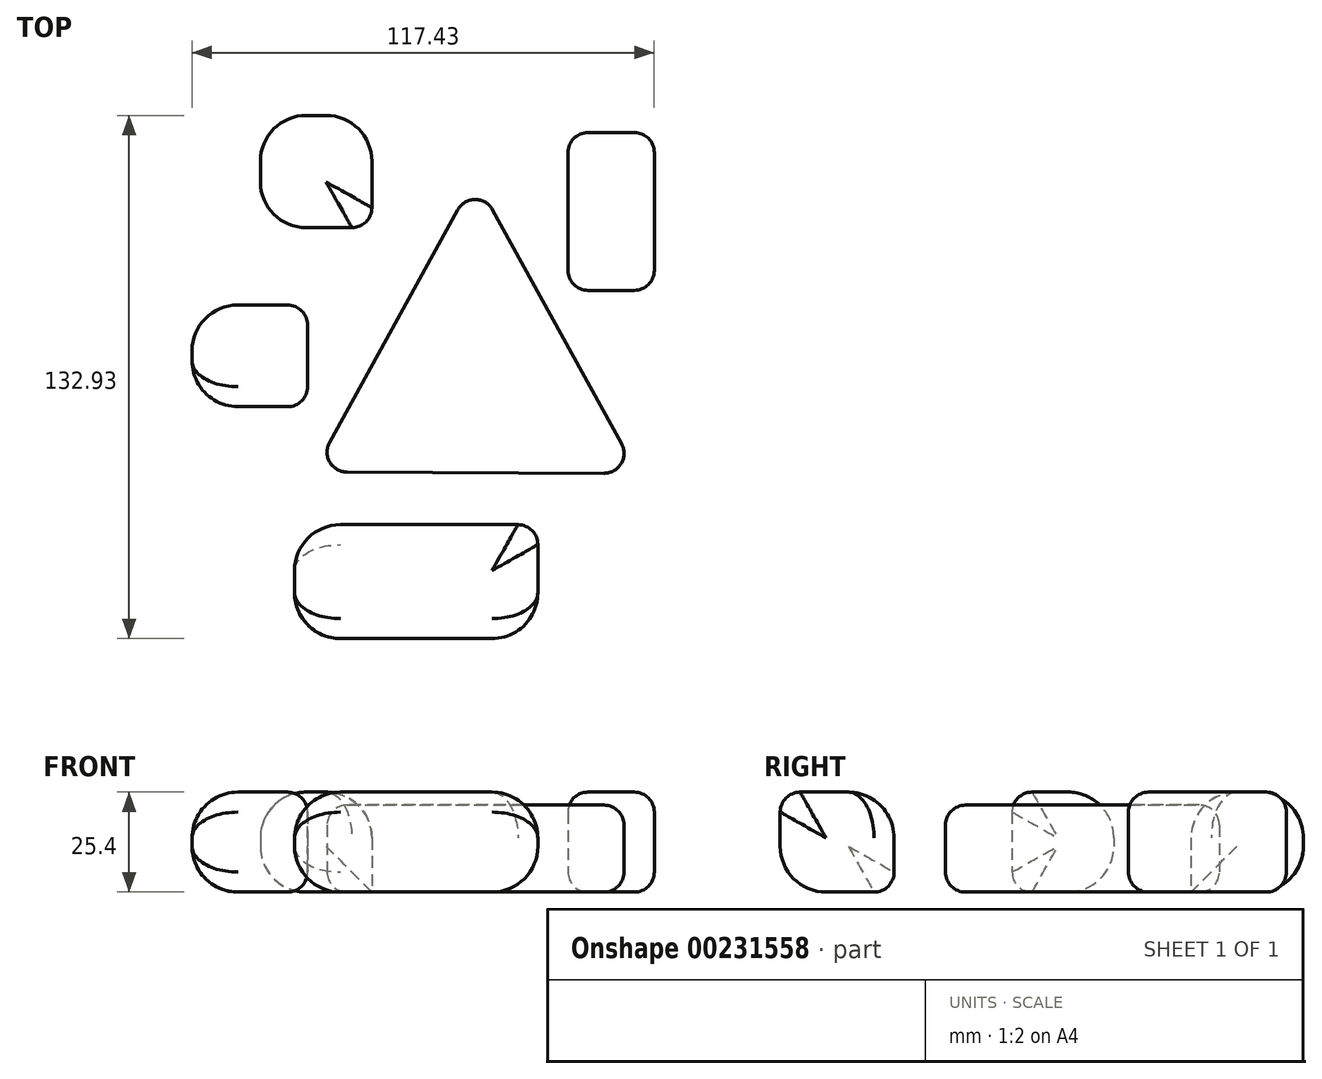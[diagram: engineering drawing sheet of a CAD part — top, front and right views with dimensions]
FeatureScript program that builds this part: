
annotation { "Feature Type Name" : "Feature", "Feature Type Description" : "" }
export const myFeature = defineFeature(function(context is Context, id is Id, definition is map)
    precondition{}
    {
        {
            var Q0;
            Q0=qCreatedBy(makeId("Top.planeOp"),FACE);
            var sketch = newSketch(context, id + "F0", { "sketchPlane" : qUnion([Q0])});
            skLineSegment(sketch, "E0.0", {"start": v(41.35, -24.6) * mm, "end": v(-41.14, -24.19) * mm});
            skLineSegment(sketch, "E0.1", {"start": v(-41.14, -24.19) * mm, "end": v(0, 50.45) * mm});
            skLineSegment(sketch, "E0.2", {"start": v(0, 50.45) * mm, "end": v(41.35, -24.6) * mm});
            skPoint(sketch, "E0.0.midPoint", {"position": v(0.1, -24.4) * mm});
            skSolve(sketch);
        }
        {
            var Q0;
            Q0=makeQuery(id+"F0.imprint","IMPRINT",FACE,{"disambiguationData":[TD([[makeQuery(id+"F0.imprint","IMPRINT",EDGE,{"derivedFrom":sQuery(id+"F0.wireOp",EDGE,"E0.0")}),-1.0]])]});
            extrude(context, id + "F1", {"entities" : qUnion([Q0]), "depth" : 22.1 * mm});
        }
        {
            var Q0;
            Q0=makeQuery(id+"F1.opExtrude","CAP_EDGE",EDGE,{"disambiguationData":[OSD([sQuery(id+"F0.wireOp",EDGE,"E0.2")])],"isStart":false});
            var Q1;
            Q1=makeQuery(id+"F1.opExtrude","CAP_EDGE",EDGE,{"disambiguationData":[OSD([sQuery(id+"F0.wireOp",EDGE,"E0.1")])],"isStart":false});
            var Q2;
            Q2=makeQuery(id+"F1.opExtrude","CAP_FACE",FACE,{"disambiguationData":[OSD([sQuery(id+"F0.wireOp",EDGE,"E0.0"),sQuery(id+"F0.wireOp",EDGE,"E0.1"),sQuery(id+"F0.wireOp",EDGE,"E0.2")])],"isStart":false});
            var Q3;
            Q3=makeQuery(id+"F1.opExtrude","CAP_EDGE",EDGE,{"disambiguationData":[OSD([sQuery(id+"F0.wireOp",EDGE,"E0.2")])],"isStart":true});
            var Q4;
            Q4=makeQuery(id+"F1.opExtrude","CAP_EDGE",EDGE,{"disambiguationData":[OSD([sQuery(id+"F0.wireOp",EDGE,"E0.0")])],"isStart":true});
            var Q5;
            Q5=makeQuery(id+"F1.opExtrude","CAP_EDGE",EDGE,{"disambiguationData":[OSD([sQuery(id+"F0.wireOp",EDGE,"E0.1")])],"isStart":true});
            var Q6;
            Q6=makeQuery(id+"F1.opExtrude","SWEPT_EDGE",EDGE,{"disambiguationData":[OSD([sQuery(id+"F0.wireOp",EDGE,"E0.0"),sQuery(id+"F0.wireOp",EDGE,"E0.1")])]});
            var Q7;
            Q7=makeQuery(id+"F1.opExtrude","SWEPT_EDGE",EDGE,{"disambiguationData":[OSD([sQuery(id+"F0.wireOp",EDGE,"E0.0"),sQuery(id+"F0.wireOp",EDGE,"E0.2")])]});
            var Q8;
            Q8=makeQuery(id+"F1.opExtrude","SWEPT_EDGE",EDGE,{"disambiguationData":[OSD([sQuery(id+"F0.wireOp",EDGE,"E0.1"),sQuery(id+"F0.wireOp",EDGE,"E0.2")])]});
            fillet(context, id + "F2", {"entities" : qUnion([Q0, Q1, Q2, Q3, Q4, Q5, Q6, Q7, Q8]), "radius" : 5.08 * mm, "tangentPropagation" : true, "allowEdgeOverflow" : false});
        }
        {
            var Q0;
            Q0=qCreatedBy(makeId("Top.planeOp"),FACE);
            var sketch = newSketch(context, id + "F3", { "sketchPlane" : qUnion([Q0])});
            skLineSegment(sketch, "E1.bottom", {"start": v(-45.9, -37.63) * mm, "end": v(15.92, -37.63) * mm});
            skLineSegment(sketch, "E1.top", {"start": v(-45.9, -66.57) * mm, "end": v(15.92, -66.57) * mm});
            skLineSegment(sketch, "E1.left", {"start": v(-45.9, -37.63) * mm, "end": v(-45.9, -66.57) * mm});
            skLineSegment(sketch, "E1.right", {"start": v(15.92, -37.63) * mm, "end": v(15.92, -66.57) * mm});
            skLineSegment(sketch, "E2.bottom", {"start": v(23.57, 62.02) * mm, "end": v(45.48, 62.02) * mm});
            skLineSegment(sketch, "E2.top", {"start": v(23.57, 21.91) * mm, "end": v(45.48, 21.91) * mm});
            skLineSegment(sketch, "E2.left", {"start": v(23.57, 62.02) * mm, "end": v(23.57, 21.91) * mm});
            skLineSegment(sketch, "E2.right", {"start": v(45.48, 62.02) * mm, "end": v(45.48, 21.91) * mm});
            skLineSegment(sketch, "E3.bottom", {"start": v(-26.26, 66.36) * mm, "end": v(-54.58, 66.36) * mm});
            skLineSegment(sketch, "E3.top", {"start": v(-26.26, 37.83) * mm, "end": v(-54.58, 37.83) * mm});
            skLineSegment(sketch, "E3.left", {"start": v(-26.26, 66.36) * mm, "end": v(-26.26, 37.83) * mm});
            skLineSegment(sketch, "E3.right", {"start": v(-54.58, 66.36) * mm, "end": v(-54.58, 37.83) * mm});
            skLineSegment(sketch, "E4.bottom", {"start": v(57.06, -7.44) * mm, "end": v(52.3, -7.44) * mm});
            skLineSegment(sketch, "E4.top", {"start": v(57.06, -41.97) * mm, "end": v(52.3, -41.97) * mm});
            skLineSegment(sketch, "E4.left", {"start": v(57.06, -7.44) * mm, "end": v(57.06, -41.97) * mm});
            skLineSegment(sketch, "E4.right", {"start": v(52.3, -7.44) * mm, "end": v(52.3, -41.97) * mm});
            skLineSegment(sketch, "E5.bottom", {"start": v(-42.59, 18.2) * mm, "end": v(-71.95, 18.2) * mm});
            skLineSegment(sketch, "E5.top", {"start": v(-42.59, -7.65) * mm, "end": v(-71.95, -7.65) * mm});
            skLineSegment(sketch, "E5.left", {"start": v(-42.59, 18.2) * mm, "end": v(-42.59, -7.65) * mm});
            skLineSegment(sketch, "E5.right", {"start": v(-71.95, 18.2) * mm, "end": v(-71.95, -7.65) * mm});
            skSolve(sketch);
        }
        {
            var Q0;
            Q0=makeQuery(id+"F3.imprint","IMPRINT",FACE,{"disambiguationData":[TD([[makeQuery(id+"F3.imprint","IMPRINT",EDGE,{"derivedFrom":sQuery(id+"F3.wireOp",EDGE,"E3.bottom")}),1.0]])]});
            var Q1;
            Q1=makeQuery(id+"F3.imprint","IMPRINT",FACE,{"disambiguationData":[TD([[makeQuery(id+"F3.imprint","IMPRINT",EDGE,{"derivedFrom":sQuery(id+"F3.wireOp",EDGE,"E5.bottom")}),1.0]])]});
            var Q2;
            Q2=makeQuery(id+"F3.imprint","IMPRINT",FACE,{"disambiguationData":[TD([[makeQuery(id+"F3.imprint","IMPRINT",EDGE,{"derivedFrom":sQuery(id+"F3.wireOp",EDGE,"E1.bottom")}),-1.0]])]});
            var Q3;
            Q3=makeQuery(id+"F3.imprint","IMPRINT",FACE,{"disambiguationData":[TD([[makeQuery(id+"F3.imprint","IMPRINT",EDGE,{"derivedFrom":sQuery(id+"F3.wireOp",EDGE,"E4.bottom")}),1.0]])]});
            var Q4;
            Q4=makeQuery(id+"F3.imprint","IMPRINT",FACE,{"disambiguationData":[TD([[makeQuery(id+"F3.imprint","IMPRINT",EDGE,{"derivedFrom":sQuery(id+"F3.wireOp",EDGE,"E2.bottom")}),-1.0]])]});
            extrude(context, id + "F4", {"entities" : qUnion([Q0, Q1, Q2, Q3, Q4]), "depth" : 25.4 * mm});
        }
        {
            var Q0;
            Q0=makeQuery(id+"F4.opExtrude","CAP_EDGE",EDGE,{"disambiguationData":[OSD([sQuery(id+"F3.wireOp",EDGE,"E3.right")])],"isStart":false});
            var Q1;
            Q1=makeQuery(id+"F4.opExtrude","CAP_EDGE",EDGE,{"disambiguationData":[OSD([sQuery(id+"F3.wireOp",EDGE,"E3.bottom")])],"isStart":false});
            var Q2;
            Q2=makeQuery(id+"F4.opExtrude","SWEPT_EDGE",EDGE,{"disambiguationData":[OSD([sQuery(id+"F3.wireOp",EDGE,"E3.bottom"),sQuery(id+"F3.wireOp",EDGE,"E3.right")])]});
            var Q3;
            Q3=makeQuery(id+"F4.opExtrude","CAP_EDGE",EDGE,{"disambiguationData":[OSD([sQuery(id+"F3.wireOp",EDGE,"E5.bottom")])],"isStart":false});
            var Q4;
            Q4=makeQuery(id+"F4.opExtrude","SWEPT_EDGE",EDGE,{"disambiguationData":[OSD([sQuery(id+"F3.wireOp",EDGE,"E5.bottom"),sQuery(id+"F3.wireOp",EDGE,"E5.right")])]});
            var Q5;
            Q5=makeQuery(id+"F4.opExtrude","CAP_EDGE",EDGE,{"disambiguationData":[OSD([sQuery(id+"F3.wireOp",EDGE,"E5.right")])],"isStart":false});
            var Q6;
            Q6=makeQuery(id+"F4.opExtrude","SWEPT_EDGE",EDGE,{"disambiguationData":[OSD([sQuery(id+"F3.wireOp",EDGE,"E1.bottom"),sQuery(id+"F3.wireOp",EDGE,"E1.left")])]});
            var Q7;
            Q7=makeQuery(id+"F4.opExtrude","CAP_EDGE",EDGE,{"disambiguationData":[OSD([sQuery(id+"F3.wireOp",EDGE,"E1.left")])],"isStart":false});
            var Q8;
            Q8=makeQuery(id+"F4.opExtrude","CAP_EDGE",EDGE,{"disambiguationData":[OSD([sQuery(id+"F3.wireOp",EDGE,"E1.bottom")])],"isStart":false});
            var Q9;
            Q9=makeQuery(id+"F4.opExtrude","CAP_EDGE",EDGE,{"disambiguationData":[OSD([sQuery(id+"F3.wireOp",EDGE,"E1.left")])],"isStart":true});
            var Q10;
            Q10=makeQuery(id+"F4.opExtrude","SWEPT_EDGE",EDGE,{"disambiguationData":[OSD([sQuery(id+"F3.wireOp",EDGE,"E1.top"),sQuery(id+"F3.wireOp",EDGE,"E1.left")])]});
            var Q11;
            Q11=makeQuery(id+"F4.opExtrude","SWEPT_FACE",FACE,{"disambiguationData":[OSD([sQuery(id+"F3.wireOp",EDGE,"E5.right")])]});
            var Q12;
            Q12=makeQuery(id+"F4.opExtrude","CAP_EDGE",EDGE,{"disambiguationData":[OSD([sQuery(id+"F3.wireOp",EDGE,"E5.bottom")])],"isStart":true});
            var Q13;
            Q13=makeQuery(id+"F4.opExtrude","CAP_EDGE",EDGE,{"disambiguationData":[OSD([sQuery(id+"F3.wireOp",EDGE,"E3.right")])],"isStart":true});
            var Q14;
            Q14=makeQuery(id+"F4.opExtrude","SWEPT_EDGE",EDGE,{"disambiguationData":[OSD([sQuery(id+"F3.wireOp",EDGE,"E3.top"),sQuery(id+"F3.wireOp",EDGE,"E3.right")])]});
            var Q15;
            Q15=makeQuery(id+"F4.opExtrude","SWEPT_EDGE",EDGE,{"disambiguationData":[OSD([sQuery(id+"F3.wireOp",EDGE,"E3.bottom"),sQuery(id+"F3.wireOp",EDGE,"E3.left")])]});
            var Q16;
            Q16=makeQuery(id+"F4.opExtrude","CAP_EDGE",EDGE,{"disambiguationData":[OSD([sQuery(id+"F3.wireOp",EDGE,"E3.bottom")])],"isStart":true});
            var Q17;
            Q17=makeQuery(id+"F4.opExtrude","CAP_EDGE",EDGE,{"disambiguationData":[OSD([sQuery(id+"F3.wireOp",EDGE,"E3.left")])],"isStart":false});
            var Q18;
            Q18=makeQuery(id+"F4.opExtrude","CAP_EDGE",EDGE,{"disambiguationData":[OSD([sQuery(id+"F3.wireOp",EDGE,"E3.top")])],"isStart":false});
            var Q19;
            Q19=makeQuery(id+"F4.opExtrude","CAP_EDGE",EDGE,{"disambiguationData":[OSD([sQuery(id+"F3.wireOp",EDGE,"E2.left")])],"isStart":false});
            var Q20;
            Q20=makeQuery(id+"F4.opExtrude","CAP_EDGE",EDGE,{"disambiguationData":[OSD([sQuery(id+"F3.wireOp",EDGE,"E2.top")])],"isStart":false});
            var Q21;
            Q21=makeQuery(id+"F4.opExtrude","CAP_EDGE",EDGE,{"disambiguationData":[OSD([sQuery(id+"F3.wireOp",EDGE,"E2.right")])],"isStart":false});
            var Q22;
            Q22=makeQuery(id+"F4.opExtrude","CAP_EDGE",EDGE,{"disambiguationData":[OSD([sQuery(id+"F3.wireOp",EDGE,"E2.bottom")])],"isStart":false});
            var Q23;
            Q23=makeQuery(id+"F4.opExtrude","SWEPT_EDGE",EDGE,{"disambiguationData":[OSD([sQuery(id+"F3.wireOp",EDGE,"E2.bottom"),sQuery(id+"F3.wireOp",EDGE,"E2.left")])]});
            var Q24;
            Q24=makeQuery(id+"F4.opExtrude","SWEPT_EDGE",EDGE,{"disambiguationData":[OSD([sQuery(id+"F3.wireOp",EDGE,"E2.top"),sQuery(id+"F3.wireOp",EDGE,"E2.left")])]});
            var Q25;
            Q25=makeQuery(id+"F4.opExtrude","CAP_EDGE",EDGE,{"disambiguationData":[OSD([sQuery(id+"F3.wireOp",EDGE,"E2.left")])],"isStart":true});
            var Q26;
            Q26=makeQuery(id+"F4.opExtrude","SWEPT_EDGE",EDGE,{"disambiguationData":[OSD([sQuery(id+"F3.wireOp",EDGE,"E2.bottom"),sQuery(id+"F3.wireOp",EDGE,"E2.right")])]});
            var Q27;
            Q27=makeQuery(id+"F4.opExtrude","CAP_EDGE",EDGE,{"disambiguationData":[OSD([sQuery(id+"F3.wireOp",EDGE,"E2.bottom")])],"isStart":true});
            var Q28;
            Q28=makeQuery(id+"F4.opExtrude","CAP_EDGE",EDGE,{"disambiguationData":[OSD([sQuery(id+"F3.wireOp",EDGE,"E1.right")])],"isStart":true});
            var Q29;
            Q29=makeQuery(id+"F4.opExtrude","CAP_EDGE",EDGE,{"disambiguationData":[OSD([sQuery(id+"F3.wireOp",EDGE,"E1.top")])],"isStart":true});
            var Q30;
            Q30=makeQuery(id+"F4.opExtrude","SWEPT_EDGE",EDGE,{"disambiguationData":[OSD([sQuery(id+"F3.wireOp",EDGE,"E1.top"),sQuery(id+"F3.wireOp",EDGE,"E1.right")])]});
            var Q31;
            Q31=makeQuery(id+"F4.opExtrude","CAP_EDGE",EDGE,{"disambiguationData":[OSD([sQuery(id+"F3.wireOp",EDGE,"E1.right")])],"isStart":false});
            var Q32;
            Q32=makeQuery(id+"F4.opExtrude","CAP_EDGE",EDGE,{"disambiguationData":[OSD([sQuery(id+"F3.wireOp",EDGE,"E4.left")])],"isStart":true});
            var Q33;
            Q33=makeQuery(id+"F4.opExtrude","CAP_EDGE",EDGE,{"disambiguationData":[OSD([sQuery(id+"F3.wireOp",EDGE,"E4.right")])],"isStart":true});
            var Q34;
            Q34=makeQuery(id+"F4.opExtrude","SWEPT_EDGE",EDGE,{"disambiguationData":[OSD([sQuery(id+"F3.wireOp",EDGE,"E4.bottom"),sQuery(id+"F3.wireOp",EDGE,"E4.right")])]});
            var Q35;
            Q35=makeQuery(id+"F4.opExtrude","SWEPT_EDGE",EDGE,{"disambiguationData":[OSD([sQuery(id+"F3.wireOp",EDGE,"E4.bottom"),sQuery(id+"F3.wireOp",EDGE,"E4.left")])]});
            var Q36;
            Q36=makeQuery(id+"F4.opExtrude","CAP_EDGE",EDGE,{"disambiguationData":[OSD([sQuery(id+"F3.wireOp",EDGE,"E4.left")])],"isStart":false});
            fillet(context, id + "F5", {"entities" : qUnion([Q0, Q1, Q2, Q3, Q4, Q5, Q6, Q7, Q8, Q9, Q10, Q11, Q12, Q13, Q14, Q15, Q16, Q17, Q18, Q19, Q20, Q21, Q22, Q23, Q24, Q25, Q26, Q27, Q28, Q29, Q30, Q31, Q32, Q33, Q34, Q35, Q36]), "radius" : 11.65 * mm, "tangentPropagation" : true, "allowEdgeOverflow" : false});
        }
        {
            var Q0;
            Q0=makeQuery(id+"F4.opExtrude","SWEPT_BODY",BODY,{"disambiguationData":[OSD([sQuery(id+"F3.wireOp",EDGE,"E4.bottom"),sQuery(id+"F3.wireOp",EDGE,"E4.top"),sQuery(id+"F3.wireOp",EDGE,"E4.left"),sQuery(id+"F3.wireOp",EDGE,"E4.right")])]});
            deleteBodies(context, id + "F6", {"entities" : qUnion([Q0])});
        }
        {
            var Q0;
            Q0=makeQuery(id+"F4.opExtrude","CAP_EDGE",EDGE,{"disambiguationData":[OSD([sQuery(id+"F3.wireOp",EDGE,"E3.right")])],"isStart":false});
            var Q1;
            Q1=makeQuery(id+"F4.opExtrude","SWEPT_EDGE",EDGE,{"disambiguationData":[OSD([sQuery(id+"F3.wireOp",EDGE,"E3.bottom"),sQuery(id+"F3.wireOp",EDGE,"E3.right")])]});
            var Q2;
            Q2=makeQuery(id+"F4.opExtrude","SWEPT_EDGE",EDGE,{"disambiguationData":[OSD([sQuery(id+"F3.wireOp",EDGE,"E3.top"),sQuery(id+"F3.wireOp",EDGE,"E3.right")])]});
            var Q3;
            Q3=makeQuery(id+"F4.opExtrude","CAP_EDGE",EDGE,{"disambiguationData":[OSD([sQuery(id+"F3.wireOp",EDGE,"E3.right")])],"isStart":true});
            var Q4;
            Q4=makeQuery(id+"F4.opExtrude","SWEPT_EDGE",EDGE,{"disambiguationData":[OSD([sQuery(id+"F3.wireOp",EDGE,"E5.bottom"),sQuery(id+"F3.wireOp",EDGE,"E5.right")])]});
            var Q5;
            Q5=makeQuery(id+"F4.opExtrude","SWEPT_EDGE",EDGE,{"disambiguationData":[OSD([sQuery(id+"F3.wireOp",EDGE,"E5.bottom"),sQuery(id+"F3.wireOp",EDGE,"E5.left")])]});
            var Q6;
            Q6=makeQuery(id+"F4.opExtrude","CAP_EDGE",EDGE,{"disambiguationData":[OSD([sQuery(id+"F3.wireOp",EDGE,"E5.left")])],"isStart":false});
            var Q7;
            Q7=makeQuery(id+"F4.opExtrude","CAP_EDGE",EDGE,{"disambiguationData":[OSD([sQuery(id+"F3.wireOp",EDGE,"E5.top")])],"isStart":false});
            var Q8;
            Q8=makeQuery(id+"F4.opExtrude","SWEPT_EDGE",EDGE,{"disambiguationData":[OSD([sQuery(id+"F3.wireOp",EDGE,"E5.top"),sQuery(id+"F3.wireOp",EDGE,"E5.right")])]});
            var Q9;
            Q9=makeQuery(id+"F4.opExtrude","CAP_EDGE",EDGE,{"disambiguationData":[OSD([sQuery(id+"F3.wireOp",EDGE,"E5.right")])],"isStart":true});
            var Q10;
            Q10=makeQuery(id+"F4.opExtrude","CAP_EDGE",EDGE,{"disambiguationData":[OSD([sQuery(id+"F3.wireOp",EDGE,"E5.right")])],"isStart":false});
            var Q11;
            Q11=makeQuery(id+"F4.opExtrude","CAP_EDGE",EDGE,{"disambiguationData":[OSD([sQuery(id+"F3.wireOp",EDGE,"E5.top")])],"isStart":true});
            var Q12;
            Q12=makeQuery(id+"F4.opExtrude","CAP_EDGE",EDGE,{"disambiguationData":[OSD([sQuery(id+"F3.wireOp",EDGE,"E5.bottom")])],"isStart":true});
            var Q13;
            Q13=makeQuery(id+"F4.opExtrude","SWEPT_EDGE",EDGE,{"disambiguationData":[OSD([sQuery(id+"F3.wireOp",EDGE,"E5.top"),sQuery(id+"F3.wireOp",EDGE,"E5.left")])]});
            var Q14;
            Q14=makeQuery(id+"F4.opExtrude","CAP_EDGE",EDGE,{"disambiguationData":[OSD([sQuery(id+"F3.wireOp",EDGE,"E2.right")])],"isStart":false});
            var Q15;
            Q15=makeQuery(id+"F4.opExtrude","CAP_EDGE",EDGE,{"disambiguationData":[OSD([sQuery(id+"F3.wireOp",EDGE,"E2.left")])],"isStart":false});
            var Q16;
            Q16=makeQuery(id+"F4.opExtrude","CAP_EDGE",EDGE,{"disambiguationData":[OSD([sQuery(id+"F3.wireOp",EDGE,"E3.left")])],"isStart":false});
            var Q17;
            Q17=makeQuery(id+"F4.opExtrude","CAP_EDGE",EDGE,{"disambiguationData":[OSD([sQuery(id+"F3.wireOp",EDGE,"E3.top")])],"isStart":false});
            var Q18;
            Q18=makeQuery(id+"F4.opExtrude","CAP_EDGE",EDGE,{"disambiguationData":[OSD([sQuery(id+"F3.wireOp",EDGE,"E3.bottom")])],"isStart":false});
            var Q19;
            Q19=makeQuery(id+"F4.opExtrude","SWEPT_EDGE",EDGE,{"disambiguationData":[OSD([sQuery(id+"F3.wireOp",EDGE,"E3.bottom"),sQuery(id+"F3.wireOp",EDGE,"E3.left")])]});
            var Q20;
            Q20=makeQuery(id+"F4.opExtrude","SWEPT_EDGE",EDGE,{"disambiguationData":[OSD([sQuery(id+"F3.wireOp",EDGE,"E3.top"),sQuery(id+"F3.wireOp",EDGE,"E3.left")])]});
            var Q21;
            Q21=makeQuery(id+"F4.opExtrude","CAP_EDGE",EDGE,{"disambiguationData":[OSD([sQuery(id+"F3.wireOp",EDGE,"E2.bottom")])],"isStart":false});
            var Q22;
            Q22=makeQuery(id+"F4.opExtrude","SWEPT_EDGE",EDGE,{"disambiguationData":[OSD([sQuery(id+"F3.wireOp",EDGE,"E2.bottom"),sQuery(id+"F3.wireOp",EDGE,"E2.right")])]});
            var Q23;
            Q23=makeQuery(id+"F4.opExtrude","CAP_EDGE",EDGE,{"disambiguationData":[OSD([sQuery(id+"F3.wireOp",EDGE,"E2.right")])],"isStart":true});
            var Q24;
            Q24=makeQuery(id+"F4.opExtrude","SWEPT_EDGE",EDGE,{"disambiguationData":[OSD([sQuery(id+"F3.wireOp",EDGE,"E2.top"),sQuery(id+"F3.wireOp",EDGE,"E2.right")])]});
            var Q25;
            Q25=makeQuery(id+"F4.opExtrude","CAP_EDGE",EDGE,{"disambiguationData":[OSD([sQuery(id+"F3.wireOp",EDGE,"E2.top")])],"isStart":false});
            var Q26;
            Q26=makeQuery(id+"F4.opExtrude","CAP_EDGE",EDGE,{"disambiguationData":[OSD([sQuery(id+"F3.wireOp",EDGE,"E2.bottom")])],"isStart":true});
            var Q27;
            Q27=makeQuery(id+"F4.opExtrude","SWEPT_EDGE",EDGE,{"disambiguationData":[OSD([sQuery(id+"F3.wireOp",EDGE,"E2.bottom"),sQuery(id+"F3.wireOp",EDGE,"E2.left")])]});
            var Q28;
            Q28=makeQuery(id+"F4.opExtrude","CAP_EDGE",EDGE,{"disambiguationData":[OSD([sQuery(id+"F3.wireOp",EDGE,"E2.left")])],"isStart":true});
            var Q29;
            Q29=makeQuery(id+"F4.opExtrude","CAP_EDGE",EDGE,{"disambiguationData":[OSD([sQuery(id+"F3.wireOp",EDGE,"E2.top")])],"isStart":true});
            var Q30;
            Q30=makeQuery(id+"F4.opExtrude","CAP_EDGE",EDGE,{"disambiguationData":[OSD([sQuery(id+"F3.wireOp",EDGE,"E5.left")])],"isStart":true});
            var Q31;
            Q31=makeQuery(id+"F4.opExtrude","SWEPT_EDGE",EDGE,{"disambiguationData":[OSD([sQuery(id+"F3.wireOp",EDGE,"E2.top"),sQuery(id+"F3.wireOp",EDGE,"E2.left")])]});
            var Q32;
            Q32=makeQuery(id+"F4.opExtrude","CAP_EDGE",EDGE,{"disambiguationData":[OSD([sQuery(id+"F3.wireOp",EDGE,"E1.top")])],"isStart":false});
            var Q33;
            Q33=makeQuery(id+"F4.opExtrude","SWEPT_EDGE",EDGE,{"disambiguationData":[OSD([sQuery(id+"F3.wireOp",EDGE,"E1.top"),sQuery(id+"F3.wireOp",EDGE,"E1.left")])]});
            var Q34;
            Q34=makeQuery(id+"F4.opExtrude","CAP_EDGE",EDGE,{"disambiguationData":[OSD([sQuery(id+"F3.wireOp",EDGE,"E1.left")])],"isStart":false});
            var Q35;
            Q35=makeQuery(id+"F4.opExtrude","CAP_EDGE",EDGE,{"disambiguationData":[OSD([sQuery(id+"F3.wireOp",EDGE,"E1.bottom")])],"isStart":false});
            var Q36;
            Q36=makeQuery(id+"F4.opExtrude","CAP_EDGE",EDGE,{"disambiguationData":[OSD([sQuery(id+"F3.wireOp",EDGE,"E1.right")])],"isStart":false});
            var Q37;
            Q37=makeQuery(id+"F4.opExtrude","SWEPT_EDGE",EDGE,{"disambiguationData":[OSD([sQuery(id+"F3.wireOp",EDGE,"E1.top"),sQuery(id+"F3.wireOp",EDGE,"E1.right")])]});
            var Q38;
            Q38=makeQuery(id+"F4.opExtrude","CAP_EDGE",EDGE,{"disambiguationData":[OSD([sQuery(id+"F3.wireOp",EDGE,"E1.top")])],"isStart":true});
            var Q39;
            Q39=makeQuery(id+"F4.opExtrude","CAP_EDGE",EDGE,{"disambiguationData":[OSD([sQuery(id+"F3.wireOp",EDGE,"E1.left")])],"isStart":true});
            var Q40;
            Q40=makeQuery(id+"F4.opExtrude","SWEPT_EDGE",EDGE,{"disambiguationData":[OSD([sQuery(id+"F3.wireOp",EDGE,"E1.bottom"),sQuery(id+"F3.wireOp",EDGE,"E1.left")])]});
            var Q41;
            Q41=makeQuery(id+"F4.opExtrude","CAP_EDGE",EDGE,{"disambiguationData":[OSD([sQuery(id+"F3.wireOp",EDGE,"E1.bottom")])],"isStart":true});
            fillet(context, id + "F7", {"entities" : qUnion([Q0, Q1, Q2, Q3, Q4, Q5, Q6, Q7, Q8, Q9, Q10, Q11, Q12, Q13, Q14, Q15, Q16, Q17, Q18, Q19, Q20, Q21, Q22, Q23, Q24, Q25, Q26, Q27, Q28, Q29, Q30, Q31, Q32, Q33, Q34, Q35, Q36, Q37, Q38, Q39, Q40, Q41]), "radius" : 5.08 * mm, "tangentPropagation" : true, "allowEdgeOverflow" : false});
        }
    });
